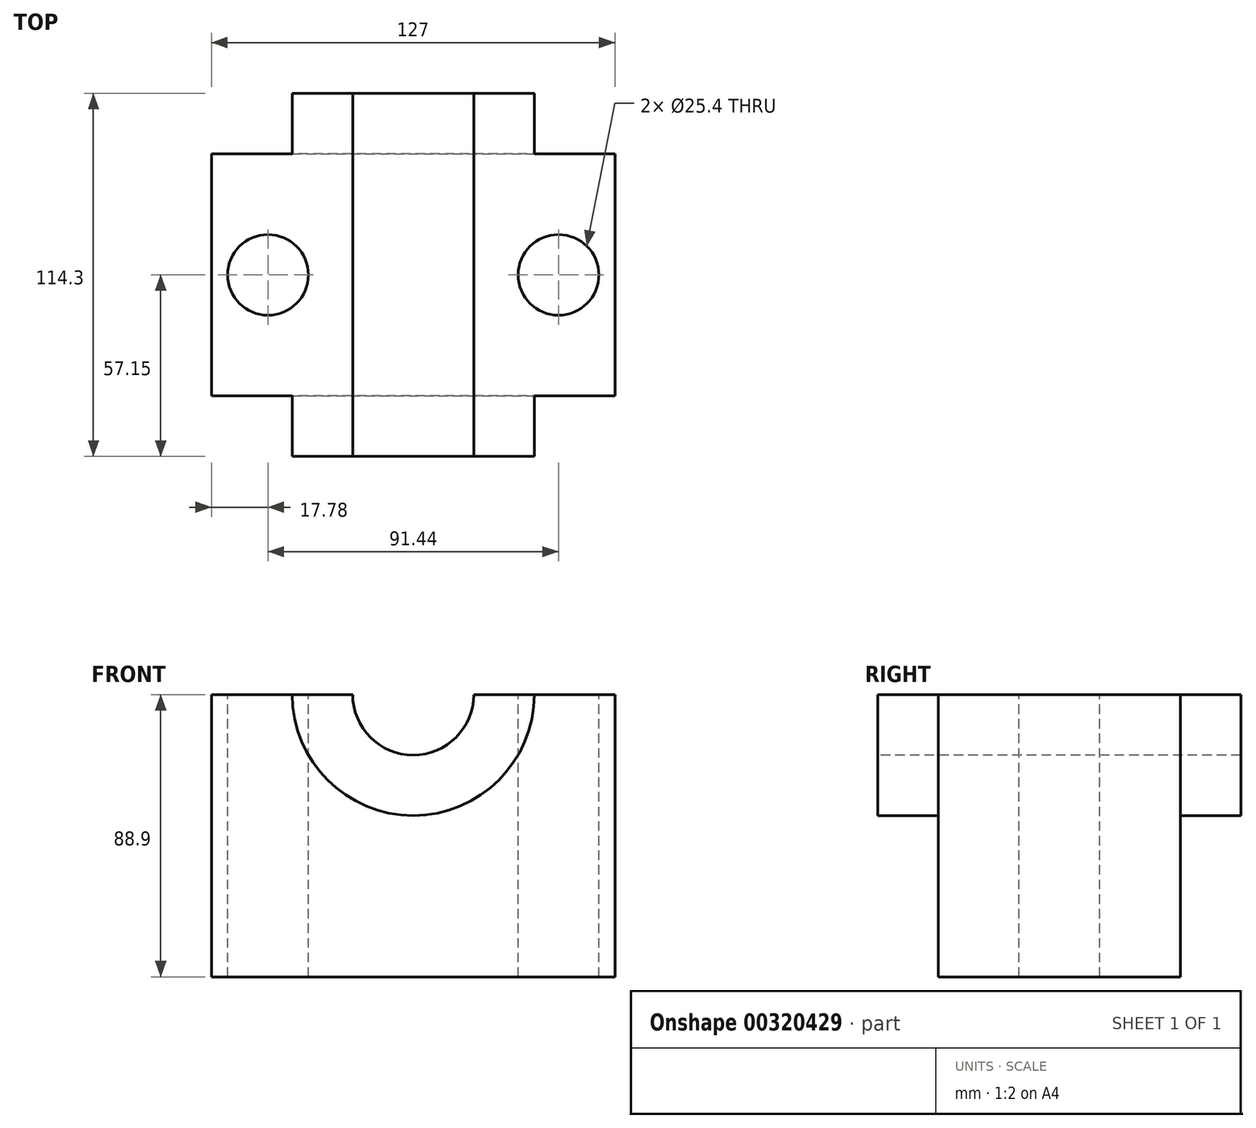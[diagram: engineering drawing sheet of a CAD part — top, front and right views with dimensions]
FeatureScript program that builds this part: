
annotation { "Feature Type Name" : "Feature", "Feature Type Description" : "" }
export const myFeature = defineFeature(function(context is Context, id is Id, definition is map)
    precondition{}
    {
        {
            var Q0;
            Q0=qCreatedBy(makeId("Top.planeOp"),FACE);
            var sketch = newSketch(context, id + "F0", { "sketchPlane" : qUnion([Q0])});
            skLineSegment(sketch, "E0.bottom", {"start": v(63.5, 38.1) * mm, "end": v(-63.5, 38.1) * mm});
            skLineSegment(sketch, "E0.top", {"start": v(63.5, -38.1) * mm, "end": v(-63.5, -38.1) * mm});
            skLineSegment(sketch, "E0.left", {"start": v(63.5, 38.1) * mm, "end": v(63.5, -38.1) * mm});
            skLineSegment(sketch, "E0.right", {"start": v(-63.5, 38.1) * mm, "end": v(-63.5, -38.1) * mm});
            skPoint(sketch, "E0.middle", {"position": v(0, 0) * mm});
            skSolve(sketch);
        }
        {
            var Q0;
            Q0=makeQuery(id+"F0.imprint","IMPRINT",FACE,{"disambiguationData":[TD([[makeQuery(id+"F0.imprint","IMPRINT",EDGE,{"derivedFrom":sQuery(id+"F0.wireOp",EDGE,"E0.bottom")}),1.0]])]});
            extrude(context, id + "F1", {"entities" : qUnion([Q0]), "depth" : 88.9 * mm});
        }
        {
            var Q0;
            Q0=qCreatedBy(makeId("Front.planeOp"),FACE);
            var sketch = newSketch(context, id + "F2", { "sketchPlane" : qUnion([Q0])});
            skCircle(sketch, "E1", {"center": v(0, 88.9) * mm, "radius": 38.1 * mm});
            skSolve(sketch);
        }
        {
            var Q0;
            Q0=makeQuery(id+"F2.imprint","IMPRINT",FACE,{"disambiguationData":[TD([[makeQuery(id+"F2.imprint","IMPRINT",EDGE,{"derivedFrom":sQuery(id+"F2.wireOp",EDGE,"E1")}),1.0]])]});
            extrude(context, id + "F3", {"entities" : qUnion([Q0]), "operationType" : NewBodyOperationType.ADD, "endBound" : BoundingType.SYMMETRIC, "depth" : 114.3 * mm});
        }
        {
            var Q0;
            Q0=qCreatedBy(makeId("Front.planeOp"),FACE);
            var sketch = newSketch(context, id + "F4", { "sketchPlane" : qUnion([Q0])});
            skLineSegment(sketch, "E2.bottom", {"start": v(-50.8, 131.58) * mm, "end": v(76.65, 131.58) * mm});
            skLineSegment(sketch, "E2.top", {"start": v(-50.8, 88.9) * mm, "end": v(76.65, 88.9) * mm});
            skLineSegment(sketch, "E2.left", {"start": v(-50.8, 131.58) * mm, "end": v(-50.8, 88.9) * mm});
            skLineSegment(sketch, "E2.right", {"start": v(76.65, 131.58) * mm, "end": v(76.65, 88.9) * mm});
            skCircle(sketch, "E3", {"center": v(0, 88.9) * mm, "radius": 19.05 * mm});
            skSolve(sketch);
        }
        {
            var Q0;
            Q0=makeQuery(id+"F4.imprint","IMPRINT",FACE,{"disambiguationData":[TD([[makeQuery(id+"F4.imprint","IMPRINT",EDGE,{"derivedFrom":sQuery(id+"F4.wireOp",EDGE,"E2.bottom")}),-1.0]])]});
            extrude(context, id + "F5", {"entities" : qUnion([Q0]), "operationType" : NewBodyOperationType.REMOVE, "endBound" : BoundingType.SYMMETRIC, "oppositeDirection" : true, "depth" : 254 * mm});
        }
        {
            var Q0;
            Q0=qCreatedBy(makeId("Front.planeOp"),FACE);
            var sketch = newSketch(context, id + "F6", { "sketchPlane" : qUnion([Q0])});
            skCircle(sketch, "E4", {"center": v(0, 88.9) * mm, "radius": 19.05 * mm});
            skSolve(sketch);
        }
        {
            var Q0;
            Q0 = qSketchRegion(id + "F6", true);
            extrude(context, id + "F7", {"entities" : qUnion([Q0]), "operationType" : NewBodyOperationType.REMOVE, "endBound" : BoundingType.SYMMETRIC, "oppositeDirection" : true, "depth" : 254 * mm});
        }
        {
            var Q0;
            {var subQ0=sQuery(id+"F4.wireOp",EDGE,"E2.top");var subQ1=sQuery(id+"F0.wireOp",EDGE,"E0.bottom");var subQ2=sQuery(id+"F0.wireOp",EDGE,"E0.right");var subQ3=sQuery(id+"F0.wireOp",EDGE,"E0.top");Q0=makeQuery(id+"F5.boolean.opBoolean","MERGE",FACE,{"derivedFrom":[makeQuery(id+"F3.boolean.opBoolean","SPLIT",FACE,{"disambiguationData":[TD([makeQuery(id+"F1.opExtrude","SWEPT_FACE",FACE,{"disambiguationData":[OSD([subQ2])]})])],"derivedFrom":makeQuery(id+"F1.opExtrude","CAP_FACE",FACE,{"disambiguationData":[OSD([subQ1,subQ3,sQuery(id+"F0.wireOp",EDGE,"E0.left"),subQ2])],"isStart":false})}),makeQuery(id+"F5.opExtrude","SWEPT_FACE",FACE,{"disambiguationData":[OSD([subQ0]),TDD([makeQuery(id+"F4.imprint","IMPRINT",EDGE,{"disambiguationData":[TD([[makeQuery(id+"F4.imprint","INTERSECT",VERTEX,{"derivedFrom":[subQ0,sQuery(id+"F4.wireOp",EDGE,"E2.left")]}),-1.0]])],"derivedFrom":subQ0})])]})]});}
            var sketch = newSketch(context, id + "F8", { "sketchPlane" : qUnion([Q0])});
            skCircle(sketch, "E5", {"center": v(-45.72, 0) * mm, "radius": 12.7 * mm});
            skCircle(sketch, "E6", {"center": v(45.72, 0) * mm, "radius": 12.7 * mm});
            skSolve(sketch);
        }
        {
            var Q0;
            Q0=makeQuery(id+"F8.imprint","IMPRINT",FACE,{"disambiguationData":[TD([[makeQuery(id+"F8.imprint","IMPRINT",EDGE,{"derivedFrom":sQuery(id+"F8.wireOp",EDGE,"E5")}),1.0]])]});
            var Q1;
            Q1=makeQuery(id+"F8.imprint","IMPRINT",FACE,{"disambiguationData":[TD([[makeQuery(id+"F8.imprint","IMPRINT",EDGE,{"derivedFrom":sQuery(id+"F8.wireOp",EDGE,"E6")}),1.0]])]});
            extrude(context, id + "F9", {"entities" : qUnion([Q0, Q1]), "operationType" : NewBodyOperationType.REMOVE, "endBound" : BoundingType.THROUGH_ALL, "oppositeDirection" : true, "depth" : 25.4 * mm});
        }
    });
